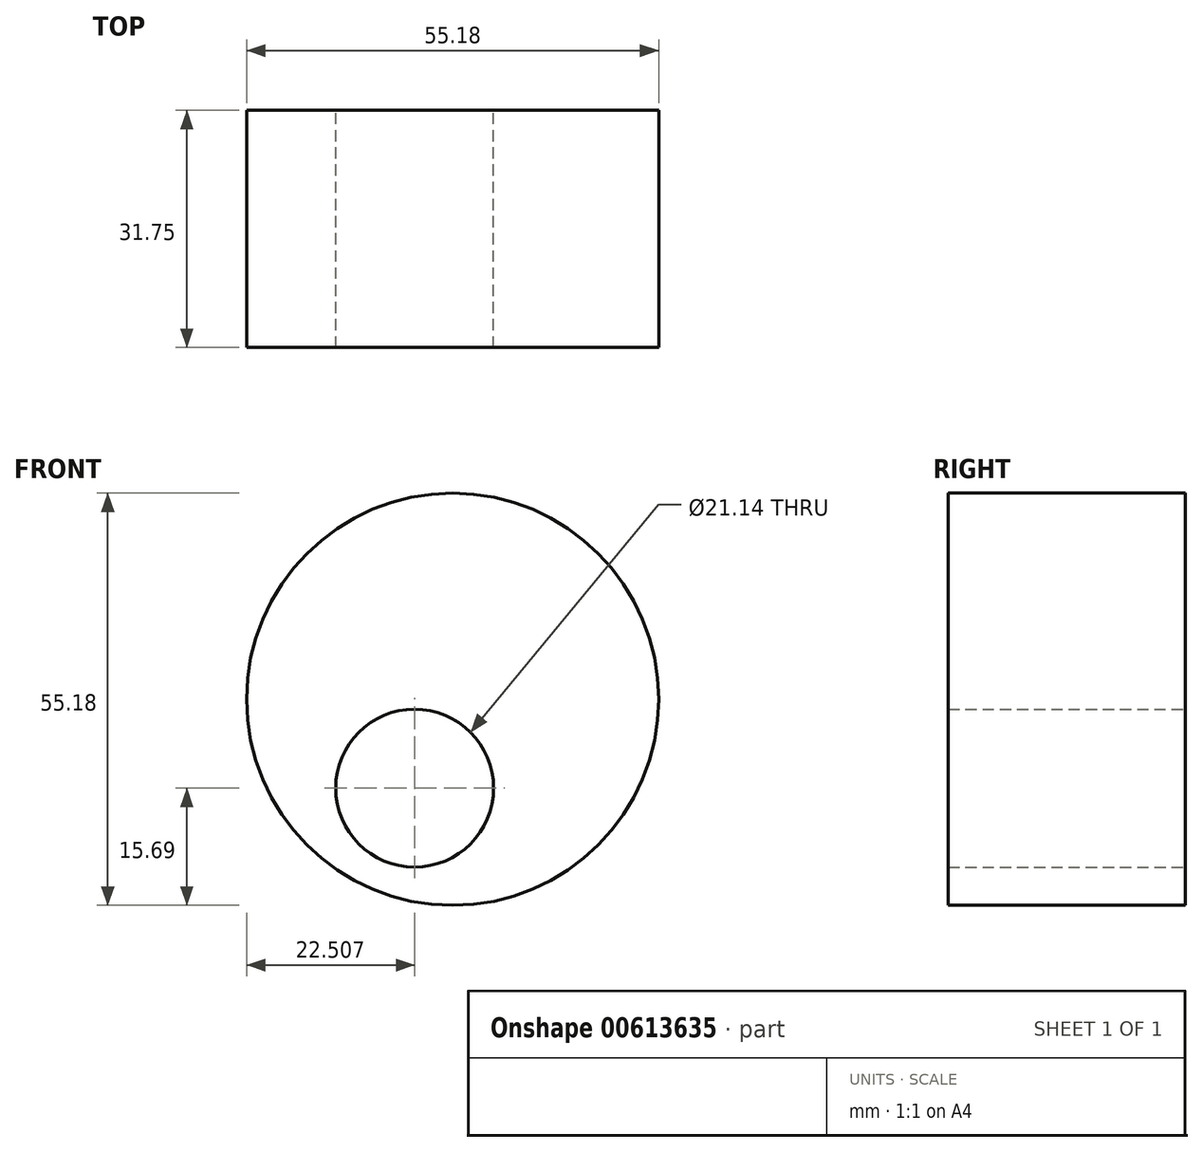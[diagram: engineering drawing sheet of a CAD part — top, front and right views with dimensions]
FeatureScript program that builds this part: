
annotation { "Feature Type Name" : "Feature", "Feature Type Description" : "" }
export const myFeature = defineFeature(function(context is Context, id is Id, definition is map)
    precondition{}
    {
        {
            var Q0;
            Q0=qCreatedBy(makeId("Front.planeOp"),FACE);
            var sketch = newSketch(context, id + "F0", { "sketchPlane" : qUnion([Q0])});
            skCircle(sketch, "E0", {"center": v(0, 0) * mm, "radius": 27.6 * mm});
            skCircle(sketch, "E1", {"center": v(-5.08, -11.9) * mm, "radius": 10.57 * mm});
            skSolve(sketch);
        }
        {
            var Q0;
            Q0 = qSketchRegion(id + "F0", true);
            extrude(context, id + "F1", {"entities" : qUnion([Q0]), "depth" : 31.75 * mm, "offsetDistance" : 25.4 * mm});
        }
    });
